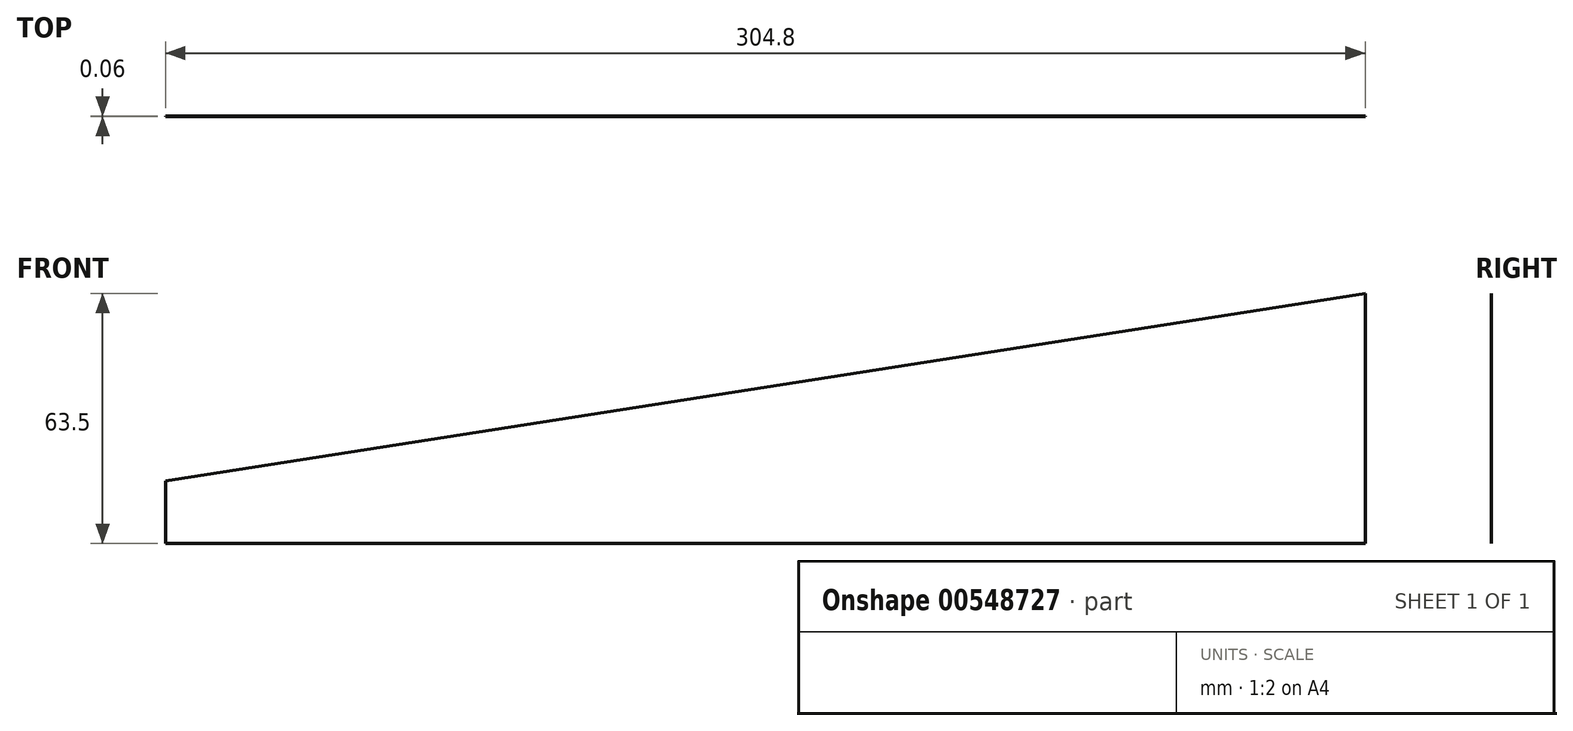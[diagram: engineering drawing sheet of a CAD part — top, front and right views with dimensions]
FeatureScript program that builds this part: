
annotation { "Feature Type Name" : "Feature", "Feature Type Description" : "" }
export const myFeature = defineFeature(function(context is Context, id is Id, definition is map)
    precondition{}
    {
        {
            var Q0;
            Q0=qCreatedBy(makeId("Front.planeOp"),FACE);
            var sketch = newSketch(context, id + "F0", { "sketchPlane" : qUnion([Q0])});
            skLineSegment(sketch, "E0.bottom", {"start": v(0, 0) * mm, "end": v(304.8, 0) * mm});
            skLineSegment(sketch, "E0.top", {"start": v(0, 63.5) * mm, "end": v(304.8, 63.5) * mm});
            skLineSegment(sketch, "E0.left", {"start": v(0, 0) * mm, "end": v(0, 63.5) * mm});
            skLineSegment(sketch, "E0.right", {"start": v(304.8, 0) * mm, "end": v(304.8, 63.5) * mm});
            skSolve(sketch);
        }
        {
            var Q0;
            Q0=makeQuery(id+"F0.imprint","IMPRINT",FACE,{"disambiguationData":[TD([[makeQuery(id+"F0.imprint","IMPRINT",EDGE,{"derivedFrom":sQuery(id+"F0.wireOp",EDGE,"E0.bottom")}),1.0]])]});
            extrude(context, id + "F1", {"entities" : qUnion([Q0]), "depth" : 25 / 406.4 * mm, "offsetDistance" : 25.4 * mm});
        }
        {
            var Q0;
            Q0=makeQuery(id+"F1.opExtrude","SWEPT_EDGE",EDGE,{"disambiguationData":[OSD([sQuery(id+"F0.wireOp",EDGE,"E0.top"),sQuery(id+"F0.wireOp",EDGE,"E0.left")])]});
            chamfer(context, id + "F2", {"entities" : qUnion([Q0]), "chamferType" : ChamferType.TWO_OFFSETS, "width1" : 47.62 * mm, "oppositeDirection" : false, "width2" : 304.8 * mm, "tangentPropagation" : true});
        }
        {
            var Q0;
            Q0=makeQuery(id+"F1.opExtrude","SWEPT_FACE",FACE,{"disambiguationData":[OSD([sQuery(id+"F0.wireOp",EDGE,"E0.right")])]});
            var sketch = newSketch(context, id + "F3", { "sketchPlane" : qUnion([Q0])});
            skCircle(sketch, "E1", {"center": v(-19.84, 19.05) * mm, "radius": 11.11 * mm});
            skSolve(sketch);
        }
        {
            var Q0;
            {var subQ0=sQuery(id+"F3.wireOp",EDGE,"E1");var subQ1=makeQuery(id+"F1.opExtrude","CAP_EDGE",EDGE,{"disambiguationData":[OSD([sQuery(id+"F0.wireOp",EDGE,"E0.right")])],"isStart":true});var subQ2=makeQuery(id+"F3.imprint","INTERSECT",VERTEX,{"disambiguationData":[OD(0.0)],"derivedFrom":[subQ1,subQ0]});Q0=makeQuery(id+"F3.imprint","IMPRINT",FACE,{"disambiguationData":[TD([[makeQuery(id+"F3.imprint","IMPRINT",EDGE,{"disambiguationData":[TD([[subQ2,1.0]])],"derivedFrom":subQ0}),1.0]])]});}
            var Q1;
            Q1=sQuery(id+"F3.wireOp",EDGE,"E1");
            extrude(context, id + "F4", {"entities" : qUnion([Q0]), "operationType" : NewBodyOperationType.REMOVE, "surfaceEntities" : qUnion([Q1]), "oppositeDirection" : true, "depth" : 50.8 * mm, "offsetDistance" : 25.4 * mm});
        }
    });
